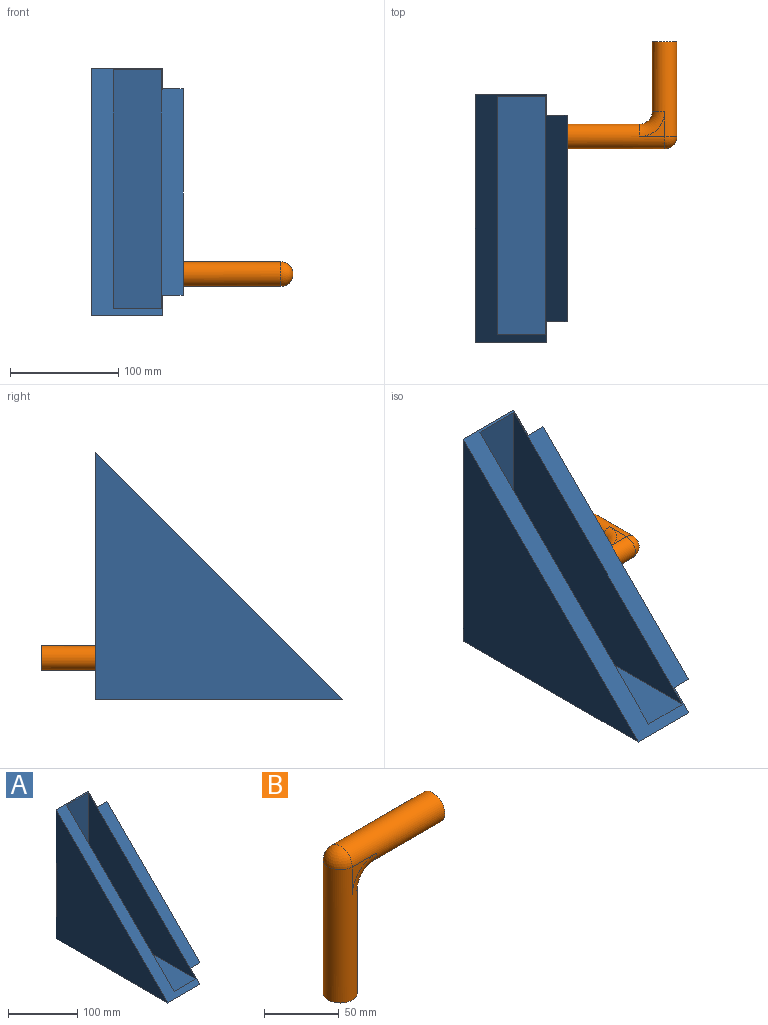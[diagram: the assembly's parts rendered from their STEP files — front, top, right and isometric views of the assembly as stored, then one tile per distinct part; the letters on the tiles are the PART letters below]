
ASSEMBLY  parts=2 mates=1
PART A: 14 faces, bbox 85.1x228.6x228.6 mm
  f0: plane 220.37x44.45mm, normal (0,0,1), area 9795.4mm2, adj f1,f2,f3,f4
  f1: plane 220.37x44.45mm, normal (0,-1,0), area 9795.4mm2, adj f0,f2,f3,f4
  f2: plane 220.37x220.37mm, normal (-1,0,0), area 24281.1mm2, adj f0,f1,f4
  f3: plane 220.37x220.37mm, normal (1,0,0), area 24281.1mm2, adj f0,f1,f4
  f4: plane 228.6x228.6mm, normal (0,-0.71,0.71), area 12629.5mm2, adj f0,f1,f2,f3,f5,f6,f7,f8
  f5: plane 228.6x228.6mm, normal (1,0,0), area 7983.9mm2, adj f4,f6,f7,f9,f10
  f6: plane 228.6x66.04mm, normal (0,1,0), area 15096.7mm2, adj f4,f5,f7,f8
  f7: plane 228.6x66.04mm, normal (0,0,-1), area 15096.7mm2, adj f4,f5,f6,f8
  f8: plane 228.6x228.6mm, normal (-1,0,0), area 26129mm2, adj f4,f6,f7
  f9: plane 190.5x19.05mm, normal (0,0,-1), area 3629mm2, adj f4,f5,f10,f11
  f10: plane 190.5x19.05mm, normal (0,1,0), area 3629mm2, adj f4,f5,f9,f11
  f11: plane 190.5x190.5mm, normal (1,0,0), area 17734.7mm2, adj f4,f9,f10,f12
  f12: cylinder r=11.43mm len=22.86mm, axis (1,0,0), area 1368.1mm2, adj f11,f13
  f13: plane 22.86x22.86mm, normal (1,0,0), area 410.4mm2, adj f12
PART B: 8 faces, bbox 99.1x22.9x120.7 mm
  f0: plane 22.86x22.86mm, normal (0,1,0), area 112.1mm2, adj f4,f6,f7
  f1: plane 22.86x22.86mm, normal (0,-1,0), area 112.1mm2, adj f4,f6,f7
  f2: plane 22.86x22.86mm, normal (0,0,-1), area 410.4mm2, adj f7
  f3: plane 22.86x22.86mm, normal (1,0,0), area 410.4mm2, adj f4
  f4: cylinder r=11.43mm len=87.63mm, axis (1,0,0), area 5472.4mm2, adj f0,f1,f3,f5,f6
  f5: sphere r=11.43mm, area 410.4mm2, adj f4,f7
  f6: torus R=22.86mm, axis (0,-1,0), area 879mm2, adj f0,f1,f4,f7
  f7: cylinder r=11.43mm len=109.22mm, axis (0,0,1), area 7023mm2, adj f0,f1,f2,f5,f6
PLACE A t=(3.78,34.25,84.91)mm
PLACE B rot(axis=(0.58,0.58,0.58),120deg) t=(50.77,235.91,111.85)mm
MATE fastened B.f7 <-> A.f12  axis (-1,0,0) through (50.77,224.48,123.28)mm
